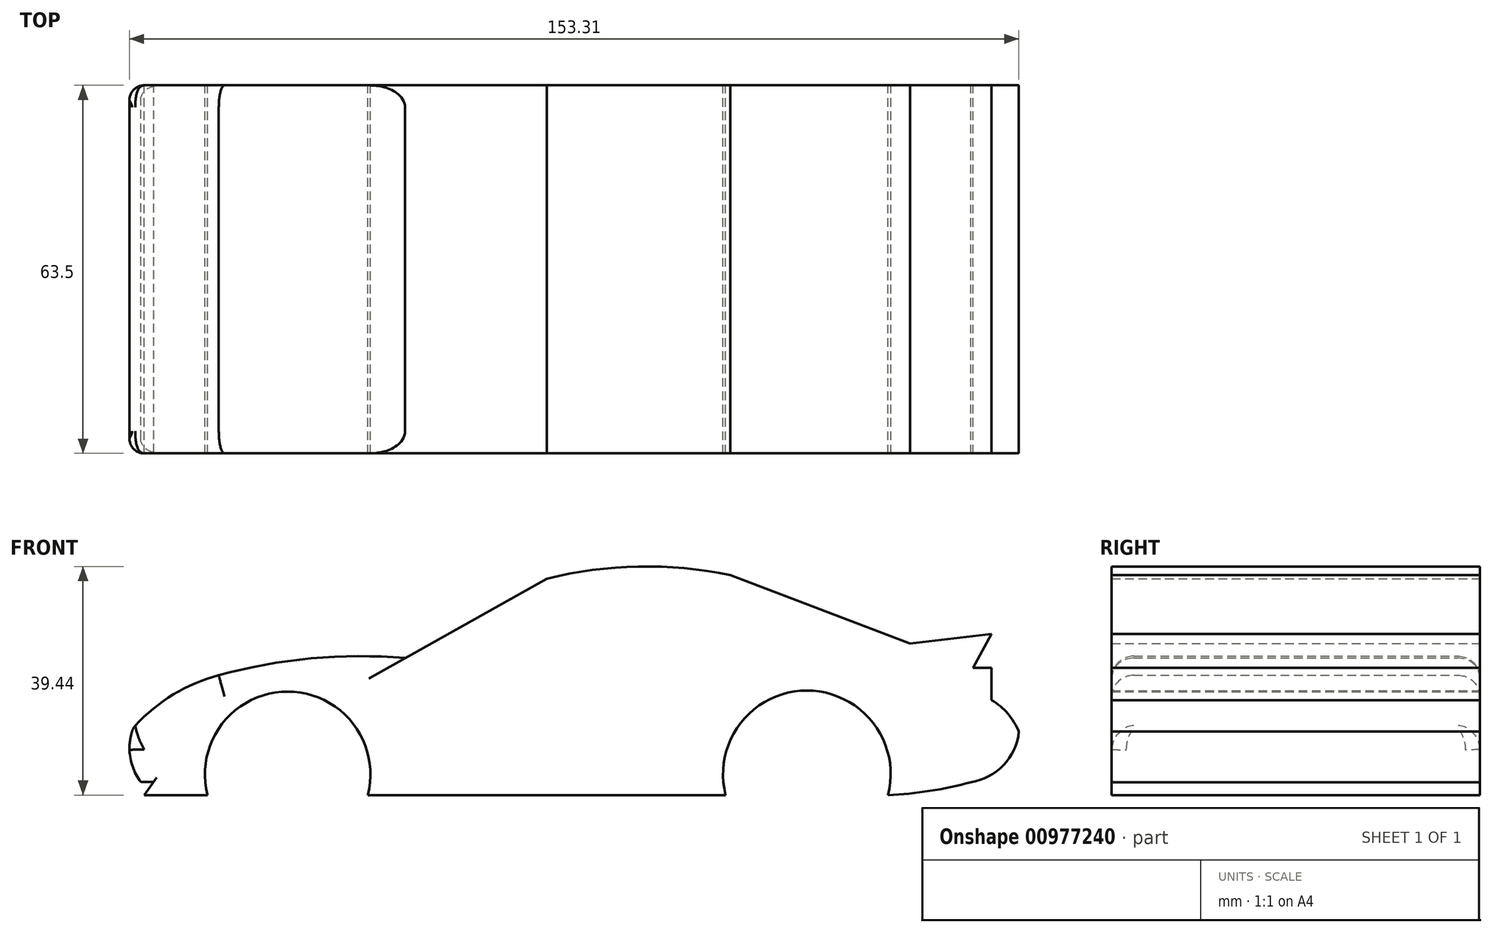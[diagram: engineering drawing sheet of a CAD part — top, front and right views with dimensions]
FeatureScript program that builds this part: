
annotation { "Feature Type Name" : "Feature", "Feature Type Description" : "" }
export const myFeature = defineFeature(function(context is Context, id is Id, definition is map)
    precondition{}
    {
        {
            var Q0;
            Q0=qCreatedBy(makeId("Front.planeOp"),FACE);
            var sketch = newSketch(context, id + "F0", { "sketchPlane" : qUnion([Q0])});
            skPoint(sketch, "E0", {"position": v(-5.22, 20.93) * mm});
            skPoint(sketch, "E1", {"position": v(26.41, 21.55) * mm});
            skPoint(sketch, "E2", {"position": v(57.42, 9.74) * mm});
            skPoint(sketch, "E3", {"position": v(71.46, 11.42) * mm});
            skPoint(sketch, "E4", {"position": v(68.3, 5.55) * mm});
            skPoint(sketch, "E5", {"position": v(71.46, 5.55) * mm});
            skPoint(sketch, "E6", {"position": v(71.46, 0) * mm});
            skPoint(sketch, "E7", {"position": v(76.17, -5.46) * mm});
            skPoint(sketch, "E8", {"position": v(67.9, -14.17) * mm});
            skPoint(sketch, "E9", {"position": v(25.61, -16.39) * mm});
            skPoint(sketch, "E10", {"position": v(-63.69, -16.39) * mm});
            skPoint(sketch, "E11", {"position": v(-74.62, -16.39) * mm});
            skPoint(sketch, "E12", {"position": v(-72.98, -14.1) * mm});
            skPoint(sketch, "E13", {"position": v(-75.2, -14.1) * mm});
            skPoint(sketch, "E14", {"position": v(-61.75, 4.27) * mm});
            skPoint(sketch, "E15", {"position": v(-76.48, -4.82) * mm});
            skLineSegment(sketch, "E16", {"start": v(26.41, 21.55) * mm, "end": v(57.42, 9.74) * mm});
            skPoint(sketch, "E17", {"position": v(-29.64, 7.24) * mm});
            skLineSegment(sketch, "E18", {"start": v(-5.22, 20.93) * mm, "end": v(-29.64, 7.24) * mm});
            skLineSegment(sketch, "E19", {"start": v(-72.98, -14.1) * mm, "end": v(-75.2, -14.1) * mm});
            skLineSegment(sketch, "E20", {"start": v(-72.98, -14.1) * mm, "end": v(-74.62, -16.39) * mm});
            skLineSegment(sketch, "E21", {"start": v(-74.62, -16.39) * mm, "end": v(-63.69, -16.39) * mm});
            skLineSegment(sketch, "E22", {"start": v(57.42, 9.74) * mm, "end": v(71.46, 11.42) * mm});
            skLineSegment(sketch, "E23", {"start": v(71.46, 11.42) * mm, "end": v(68.3, 5.55) * mm});
            skLineSegment(sketch, "E24", {"start": v(68.3, 5.55) * mm, "end": v(71.46, 5.55) * mm});
            skLineSegment(sketch, "E25", {"start": v(71.46, 5.55) * mm, "end": v(71.46, 0) * mm});
            skLineSegment(sketch, "E26", {"start": v(0, -16.39) * mm, "end": v(25.61, -16.39) * mm});
            skLineSegment(sketch, "E27", {"start": v(-36.14, -16.39) * mm, "end": v(0, -16.39) * mm});
            skArc(sketch, "E28", {"start": v(-63.69, -16.39) * mm, "mid": v(-49.88, 1.44) * mm, "end": v(-36.07, -16.39) * mm});
            skArc(sketch, "E29", {"start": v(25.61, -16.39) * mm, "mid": v(39.62, 1.64) * mm, "end": v(53.63, -16.39) * mm});
            skArc(sketch, "E30", {"start": v(26.41, 21.55) * mm, "mid": v(10.56, 23.04) * mm, "end": v(-5.22, 20.93) * mm});
            skArc(sketch, "E31", {"start": v(-29.64, 7.24) * mm, "mid": v(-45.82, 7.18) * mm, "end": v(-61.75, 4.27) * mm});
            skArc(sketch, "E32", {"start": v(-61.75, 4.27) * mm, "mid": v(-69.8, 0.83) * mm, "end": v(-76.48, -4.82) * mm});
            skArc(sketch, "E33", {"start": v(67.9, -14.17) * mm, "mid": v(73.52, -11.22) * mm, "end": v(76.17, -5.46) * mm});
            skArc(sketch, "E34", {"start": v(53.63, -16.39) * mm, "mid": v(60.83, -15.67) * mm, "end": v(67.9, -14.17) * mm});
            skArc(sketch, "E35", {"start": v(76.17, -5.46) * mm, "mid": v(74.27, -2.34) * mm, "end": v(71.46, 0) * mm});
            skArc(sketch, "E36", {"start": v(-76.48, -4.82) * mm, "mid": v(-77.05, -9.63) * mm, "end": v(-75.2, -14.1) * mm});
            skSolve(sketch);
        }
        {
            var Q0;
            Q0=makeQuery(id+"F0.imprint","IMPRINT",FACE,{"disambiguationData":[TD([[makeQuery(id+"F0.imprint","IMPRINT",EDGE,{"derivedFrom":sQuery(id+"F0.wireOp",EDGE,"E16")}),-1.0]])]});
            extrude(context, id + "F1", {"entities" : qUnion([Q0]), "depth" : 63.5 * mm, "offsetDistance" : 25.4 * mm});
        }
        {
            var Q0;
            Q0=makeQuery(id+"F1.opExtrude","CAP_EDGE",EDGE,{"disambiguationData":[OSD([sQuery(id+"F0.wireOp",EDGE,"E32")])],"isStart":false});
            var Q1;
            Q1=makeQuery(id+"F1.opExtrude","CAP_EDGE",EDGE,{"disambiguationData":[OSD([sQuery(id+"F0.wireOp",EDGE,"E31")])],"isStart":true});
            var Q2;
            Q2=makeQuery(id+"F1.opExtrude","CAP_EDGE",EDGE,{"disambiguationData":[OSD([sQuery(id+"F0.wireOp",EDGE,"E32")])],"isStart":true});
            var Q3;
            Q3=makeQuery(id+"F1.opExtrude","CAP_EDGE",EDGE,{"disambiguationData":[OSD([sQuery(id+"F0.wireOp",EDGE,"E31")])],"isStart":false});
            fillet(context, id + "F2", {"entities" : qUnion([Q0, Q1, Q2, Q3]), "radius" : 3.8 * mm, "tangentPropagation" : true, "allowEdgeOverflow" : false});
        }
        {
            var Q0;
            Q0=makeQuery(id+"F2.opFillet","BLEND_EDGE",EDGE,{"blendedFrom":[makeQuery(id+"F1.opExtrude","CAP_EDGE",EDGE,{"disambiguationData":[OSD([sQuery(id+"F0.wireOp",EDGE,"E32")])],"isStart":true}),makeQuery(id+"F1.opExtrude","SWEPT_FACE",FACE,{"disambiguationData":[OSD([sQuery(id+"F0.wireOp",EDGE,"E36")])]})],"blendedInto":[makeQuery(id+"F1.opExtrude","SWEPT_FACE",FACE,{"disambiguationData":[OSD([sQuery(id+"F0.wireOp",EDGE,"E36")])]})]});
            var Q1;
            Q1=makeQuery(id+"F2.opFillet","BLEND_EDGE",EDGE,{"blendedFrom":[makeQuery(id+"F1.opExtrude","CAP_EDGE",EDGE,{"disambiguationData":[OSD([sQuery(id+"F0.wireOp",EDGE,"E32")])],"isStart":false}),makeQuery(id+"F1.opExtrude","SWEPT_FACE",FACE,{"disambiguationData":[OSD([sQuery(id+"F0.wireOp",EDGE,"E36")])]})],"blendedInto":[makeQuery(id+"F1.opExtrude","SWEPT_FACE",FACE,{"disambiguationData":[OSD([sQuery(id+"F0.wireOp",EDGE,"E36")])]})]});
            fillet(context, id + "F3", {"entities" : qUnion([Q0, Q1]), "radius" : 2.54 * mm, "tangentPropagation" : true, "allowEdgeOverflow" : false});
        }
    });
